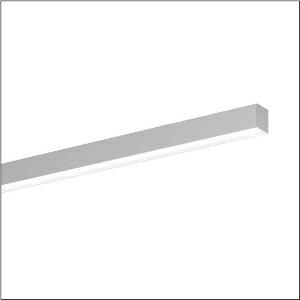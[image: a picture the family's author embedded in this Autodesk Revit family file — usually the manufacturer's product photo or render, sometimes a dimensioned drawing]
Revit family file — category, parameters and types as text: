
# Revit family: silica_r__21_51mx20tct5s_f80a
name_source: partatom
category: Lighting Fixtures
units: mm (PartAtom-declared; Revit-internal decimal feet)

## family parameters
Cut with Voids When Loaded = No
Host = Face
Light Source = No
Part Type = Normal
Room Calculation Point = No
Round Connector Dimension = Use Diameter
Shared = No

## types (1)
- --- (1 x LED, 6000 lm, 51.3 W, 6500K)
    Apparent Load = 51 VA
    CIE Flux Codes = 48 79 96 100 100
    Color Rendering = 80
    Color Temperature = 6500K
    Default Elevation = 1800 mm
    Description = Silica® 21, office luminaire, primary optical cover: cover, of PMMA, opal, light emission: direct distribution, primary light characteristic: symmetric, installation type: surface-mounted, LED, rated luminous flux: 6.000lm, luminous efficacy: 112lm/W, light colour: 8tw, colour temperature: 2700..6500K, control gear: ECG DALI, with terminal, 3+2-pole, max. 2.5mm², mains connection: 220..240V, AC, 50/60Hz, rated input power: 53.8W, luminaire housing, of aluminium, metallic grey (RAL 9006), length: 3.004mm, width: 53mm, height: 53mm, protection rating (complete): IP20, insulation class (complete): insulation class I (protective earthing), certification: CE, permissible operating ambient temperature: 0..+35°C, standard: EN 50419, packaging unit: 1 piece
    Height = 0 mm  [stored 0 ft]
    Lamp = 1 x LED
    Lamp Light Flux = 6000 lm
    Lamp Power = 51.3 W
    Lamp count = 1
    Length = 3004 mm
    Luminous efficacy = 117 lm/W
    Manufacturer = Siteco
    ModVariant = No
    Model = 51MX20TCT5S
    Mounting Place = Ceiling
    Mounting Type = Recessed
    Number of Poles = 1
    OnlyDefault = Yes
    Power Factor = 1
    Product Name = Silica® 21
    Product group = office luminaire | ceiling recessed
    ProductGroupID = 401
    Protection Class = Protection class I
    Protection Degree = IP 20
    RLX_Detail_Level = 1
    RLX_Emergency_Light_Flux = 0 lm
    RLX_Emergency_Type = 0
    RLX_Emergency_Type_DB = No
    RlxData = <blob elided: 23141 chars, md5=641b6d36>
    Socket = socket
    Standby Power = 0 W
    System Light Flux = 6000 lm
    System Power = 51 W
    Type Comments = individual setting
    Type Image = l_1313588.jpg
    URL = http://relux.com
    VarID = @adj_089031
    Voltage = 0 V
    Weight = 0.00 kg
    Width = 53 mm

note: [stored X ft] marks values corroborated as IEEE doubles in the binary element streams (Revit-internal decimal feet)

## geometry (parser evidence)
native form markers: Blend x4, Sweep x11
no freeform markers — native parametric forms only
